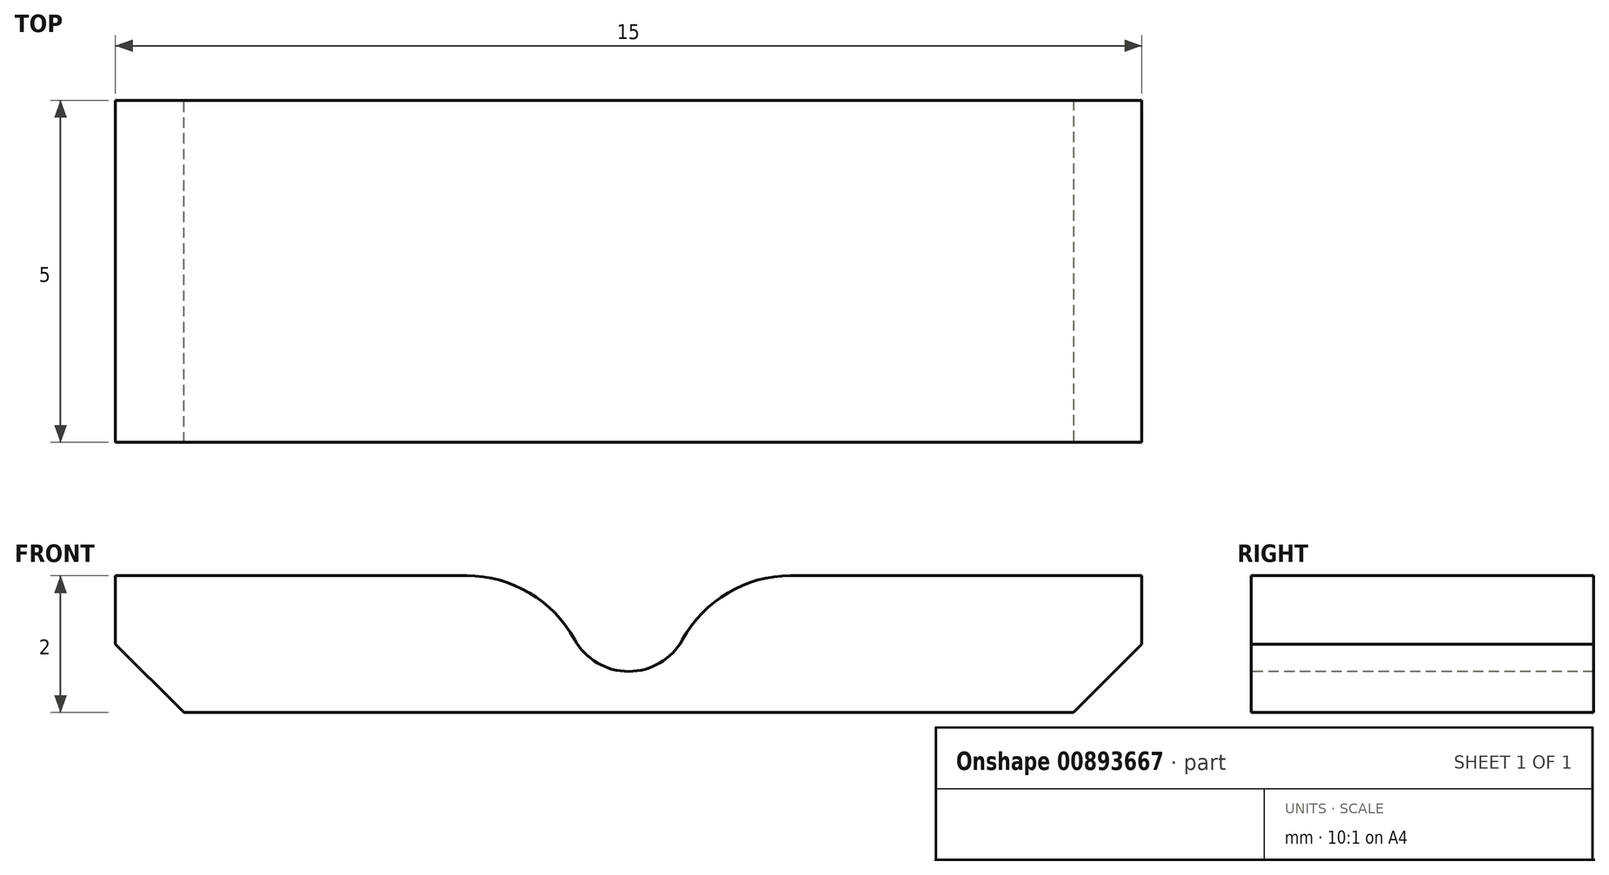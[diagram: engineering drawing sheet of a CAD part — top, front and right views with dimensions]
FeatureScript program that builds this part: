
annotation { "Feature Type Name" : "Feature", "Feature Type Description" : "" }
export const myFeature = defineFeature(function(context is Context, id is Id, definition is map)
    precondition{}
    {
        {
            var Q0;
            Q0=qCreatedBy(makeId("Top.planeOp"),FACE);
            var sketch = newSketch(context, id + "F0", { "sketchPlane" : qUnion([Q0])});
            skLineSegment(sketch, "E0.bottom", {"start": v(7.5, -2.5) * mm, "end": v(-7.5, -2.5) * mm});
            skLineSegment(sketch, "E0.top", {"start": v(7.5, 2.5) * mm, "end": v(-7.5, 2.5) * mm});
            skLineSegment(sketch, "E0.left", {"start": v(7.5, -2.5) * mm, "end": v(7.5, 2.5) * mm});
            skLineSegment(sketch, "E0.right", {"start": v(-7.5, -2.5) * mm, "end": v(-7.5, 2.5) * mm});
            skPoint(sketch, "E0.middle", {"position": v(0, 0) * mm});
            skSolve(sketch);
        }
        {
            var Q0;
            Q0 = qSketchRegion(id + "F0", true);
            extrude(context, id + "F1", {"entities" : qUnion([Q0]), "depth" : 2 * mm, "offsetDistance" : 25 * mm});
        }
        {
            var Q0;
            Q0=makeQuery(id+"F1.opExtrude","SWEPT_FACE",FACE,{"disambiguationData":[OSD([sQuery(id+"F0.wireOp",EDGE,"E0.bottom")])]});
            var sketch = newSketch(context, id + "F2", { "sketchPlane" : qUnion([Q0])});
            skPoint(sketch, "E1", {"position": v(0, 0.6) * mm});
            skArc(sketch, "E2", {"start": v(-0.79, 1.07) * mm, "mid": v(0, 0.6) * mm, "end": v(0.79, 1.07) * mm});
            skLineSegment(sketch, "E3.0", {"start": v(7.5, 2) * mm, "end": v(-7.5, 2) * mm});
            skArc(sketch, "E4", {"start": v(-0.79, 1.07) * mm, "mid": v(-1.45, 1.75) * mm, "end": v(-2.37, 2) * mm});
            skLineSegment(sketch, "E5", {"start": v(0, 0.97) * mm, "end": v(0, 1.75) * mm});
            skPoint(sketch, "E5.endSnap0", {"position": v(0, 2) * mm});
            skArc(sketch, "E6.MirrorC", {"start": v(0.79, 1.07) * mm, "mid": v(1.45, 1.75) * mm, "end": v(2.37, 2) * mm});
            skLineSegment(sketch, "E7.bottom", {"start": v(-2.37, 2) * mm, "end": v(2.37, 2) * mm});
            skLineSegment(sketch, "E7.top", {"start": v(-2.37, 2.54) * mm, "end": v(2.37, 2.54) * mm});
            skLineSegment(sketch, "E7.left", {"start": v(-2.37, 2) * mm, "end": v(-2.37, 2.54) * mm});
            skLineSegment(sketch, "E7.right", {"start": v(2.37, 2) * mm, "end": v(2.37, 2.54) * mm});
            skSolve(sketch);
        }
        {
            var Q0;
            Q0 = qSketchRegion(id + "F2", true);
            extrude(context, id + "F3", {"entities" : qUnion([Q0]), "operationType" : NewBodyOperationType.REMOVE, "endBound" : BoundingType.THROUGH_ALL, "oppositeDirection" : true, "depth" : 25 * mm, "offsetDistance" : 25 * mm});
        }
        {
            var Q0;
            Q0=makeQuery(id+"F1.opExtrude","CAP_EDGE",EDGE,{"disambiguationData":[OSD([sQuery(id+"F0.wireOp",EDGE,"E0.right")])],"isStart":true});
            var Q1;
            Q1=makeQuery(id+"F1.opExtrude","CAP_EDGE",EDGE,{"disambiguationData":[OSD([sQuery(id+"F0.wireOp",EDGE,"E0.left")])],"isStart":true});
            chamfer(context, id + "F4", {"entities" : qUnion([Q0, Q1]), "width" : 1 * mm, "tangentPropagation" : true});
        }
    });
